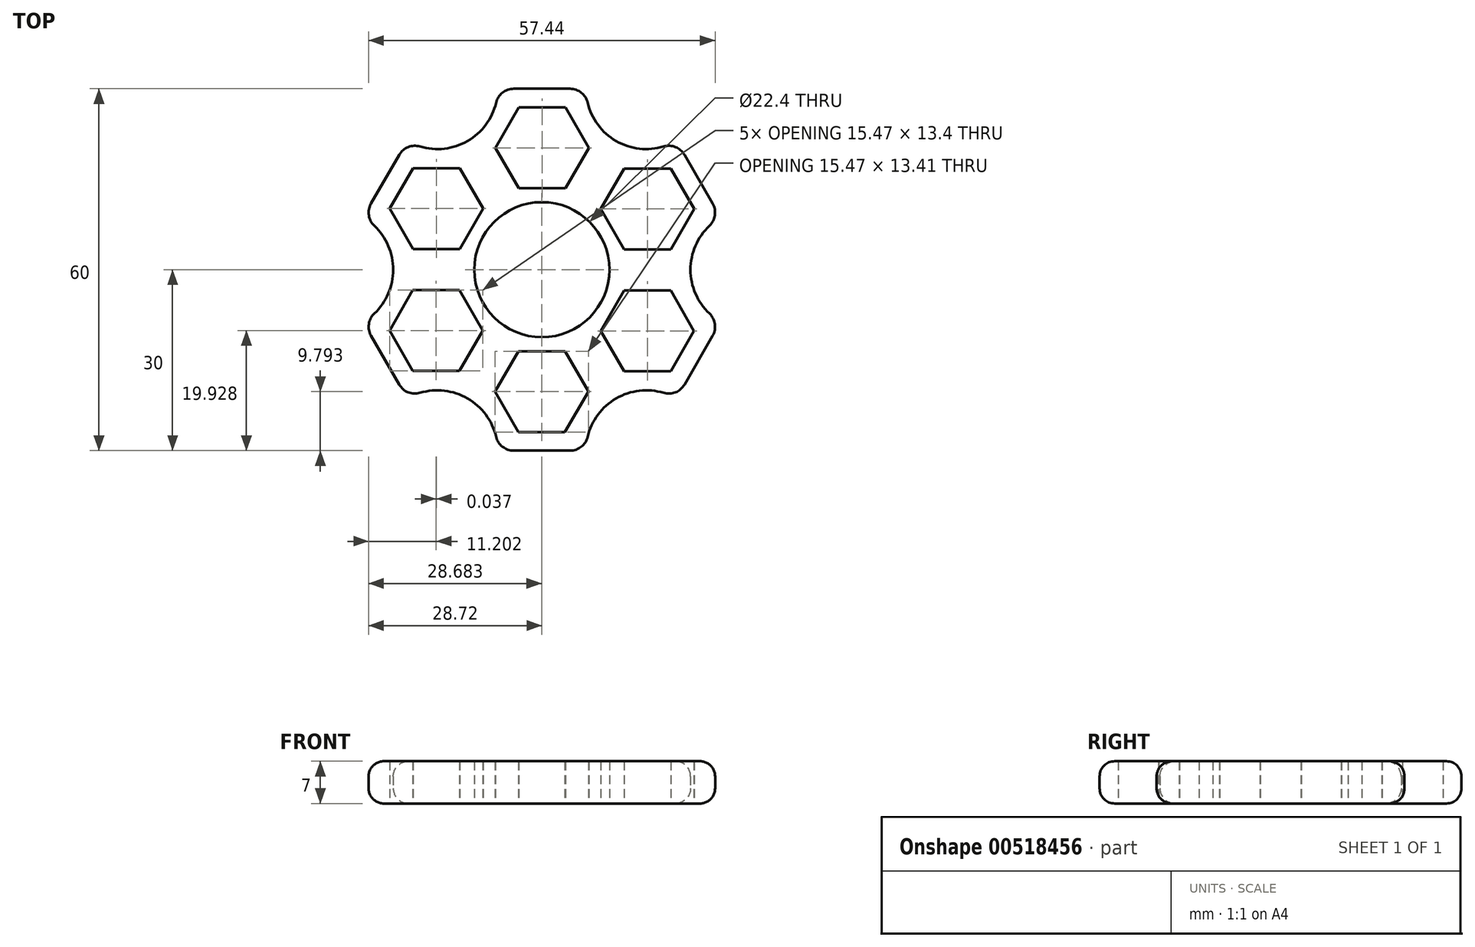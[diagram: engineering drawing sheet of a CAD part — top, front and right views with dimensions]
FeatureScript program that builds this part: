
annotation { "Feature Type Name" : "Feature", "Feature Type Description" : "" }
export const myFeature = defineFeature(function(context is Context, id is Id, definition is map)
    precondition{}
    {
        {
            var Q0;
            Q0=qCreatedBy(makeId("Top.planeOp"),FACE);
            var sketch = newSketch(context, id + "F0", { "sketchPlane" : qUnion([Q0])});
            skCircle(sketch, "E0", {"center": v(0, 0) * mm, "radius": 11.2 * mm});
            skCircle(sketch, "E1.cCircle", {"center": v(0, 0) * mm, "radius": 17.5 * mm, "construction": true});
            skLineSegment(sketch, "E1.0", {"start": v(0.04, 20.2) * mm, "end": v(17.52, 10.07) * mm});
            skLineSegment(sketch, "E1.1", {"start": v(17.52, 10.07) * mm, "end": v(17.48, -10.14) * mm});
            skLineSegment(sketch, "E1.2", {"start": v(17.48, -10.14) * mm, "end": v(-0.04, -20.2) * mm});
            skLineSegment(sketch, "E1.3", {"start": v(-0.04, -20.2) * mm, "end": v(-17.52, -10.07) * mm});
            skLineSegment(sketch, "E1.4", {"start": v(-17.52, -10.07) * mm, "end": v(-17.48, 10.14) * mm});
            skLineSegment(sketch, "E1.5", {"start": v(-17.48, 10.14) * mm, "end": v(0.04, 20.2) * mm});
            skPoint(sketch, "E1.0.midPoint", {"position": v(8.78, 15.14) * mm});
            skCircle(sketch, "E2.cCircle", {"center": v(0.04, 20.2) * mm, "radius": 6.7 * mm, "construction": true});
            skLineSegment(sketch, "E2.0", {"start": v(-3.83, 26.9) * mm, "end": v(3.9, 26.9) * mm});
            skLineSegment(sketch, "E2.1", {"start": v(3.9, 26.9) * mm, "end": v(7.77, 20.2) * mm});
            skLineSegment(sketch, "E2.2", {"start": v(7.77, 20.2) * mm, "end": v(3.9, 13.5) * mm});
            skLineSegment(sketch, "E2.3", {"start": v(3.9, 13.5) * mm, "end": v(-3.83, 13.5) * mm});
            skLineSegment(sketch, "E2.4", {"start": v(-3.83, 13.5) * mm, "end": v(-7.7, 20.2) * mm});
            skLineSegment(sketch, "E2.5", {"start": v(-7.7, 20.2) * mm, "end": v(-3.83, 26.9) * mm});
            skPoint(sketch, "E2.0.midPoint", {"position": v(0.04, 26.9) * mm});
            skCircle(sketch, "E3.cCircle", {"center": v(-17.48, 10.14) * mm, "radius": 6.7 * mm, "construction": true});
            skLineSegment(sketch, "E3.0", {"start": v(-21.35, 16.84) * mm, "end": v(-13.61, 16.84) * mm});
            skLineSegment(sketch, "E3.1", {"start": v(-13.61, 16.84) * mm, "end": v(-9.75, 10.14) * mm});
            skLineSegment(sketch, "E3.2", {"start": v(-9.75, 10.14) * mm, "end": v(-13.61, 3.44) * mm});
            skLineSegment(sketch, "E3.3", {"start": v(-13.61, 3.44) * mm, "end": v(-21.35, 3.44) * mm});
            skLineSegment(sketch, "E3.4", {"start": v(-21.35, 3.44) * mm, "end": v(-25.22, 10.14) * mm});
            skLineSegment(sketch, "E3.5", {"start": v(-25.22, 10.14) * mm, "end": v(-21.35, 16.84) * mm});
            skPoint(sketch, "E3.0.midPoint", {"position": v(-17.48, 16.84) * mm});
            skCircle(sketch, "E4.cCircle", {"center": v(-17.52, -10.07) * mm, "radius": 6.7 * mm, "construction": true});
            skLineSegment(sketch, "E4.0", {"start": v(-13.65, -16.77) * mm, "end": v(-21.39, -16.77) * mm});
            skLineSegment(sketch, "E4.1", {"start": v(-21.39, -16.77) * mm, "end": v(-25.25, -10.07) * mm});
            skLineSegment(sketch, "E4.2", {"start": v(-25.25, -10.07) * mm, "end": v(-21.39, -3.37) * mm});
            skLineSegment(sketch, "E4.3", {"start": v(-21.39, -3.37) * mm, "end": v(-13.65, -3.37) * mm});
            skLineSegment(sketch, "E4.4", {"start": v(-13.65, -3.37) * mm, "end": v(-9.78, -10.07) * mm});
            skLineSegment(sketch, "E4.5", {"start": v(-9.78, -10.07) * mm, "end": v(-13.65, -16.77) * mm});
            skPoint(sketch, "E4.0.midPoint", {"position": v(-17.52, -16.77) * mm});
            skCircle(sketch, "E5.cCircle", {"center": v(17.48, -10.14) * mm, "radius": 6.7 * mm, "construction": true});
            skLineSegment(sketch, "E5.0", {"start": v(21.35, -16.84) * mm, "end": v(13.61, -16.84) * mm});
            skLineSegment(sketch, "E5.1", {"start": v(13.61, -16.84) * mm, "end": v(9.75, -10.14) * mm});
            skLineSegment(sketch, "E5.2", {"start": v(9.75, -10.14) * mm, "end": v(13.61, -3.44) * mm});
            skLineSegment(sketch, "E5.3", {"start": v(13.61, -3.44) * mm, "end": v(21.35, -3.44) * mm});
            skLineSegment(sketch, "E5.4", {"start": v(21.35, -3.44) * mm, "end": v(25.22, -10.14) * mm});
            skLineSegment(sketch, "E5.5", {"start": v(25.22, -10.14) * mm, "end": v(21.35, -16.84) * mm});
            skPoint(sketch, "E5.0.midPoint", {"position": v(17.48, -16.84) * mm});
            skCircle(sketch, "E6.cCircle", {"center": v(-0.04, -20.2) * mm, "radius": 6.7 * mm, "construction": true});
            skLineSegment(sketch, "E6.0", {"start": v(-3.9, -13.5) * mm, "end": v(3.84, -13.51) * mm});
            skLineSegment(sketch, "E6.1", {"start": v(3.84, -13.51) * mm, "end": v(7.7, -20.22) * mm});
            skLineSegment(sketch, "E6.2", {"start": v(7.7, -20.22) * mm, "end": v(3.82, -26.91) * mm});
            skLineSegment(sketch, "E6.3", {"start": v(3.82, -26.91) * mm, "end": v(-3.92, -26.9) * mm});
            skLineSegment(sketch, "E6.4", {"start": v(-3.92, -26.9) * mm, "end": v(-7.77, -20.2) * mm});
            skLineSegment(sketch, "E6.5", {"start": v(-7.77, -20.2) * mm, "end": v(-3.9, -13.5) * mm});
            skPoint(sketch, "E6.0.midPoint", {"position": v(-0.02, -13.5) * mm});
            skCircle(sketch, "E7.cCircle", {"center": v(17.52, 10.07) * mm, "radius": 6.7 * mm, "construction": true});
            skLineSegment(sketch, "E7.0", {"start": v(21.39, 16.77) * mm, "end": v(25.25, 10.07) * mm});
            skLineSegment(sketch, "E7.1", {"start": v(25.25, 10.07) * mm, "end": v(21.39, 3.37) * mm});
            skLineSegment(sketch, "E7.2", {"start": v(21.39, 3.37) * mm, "end": v(13.65, 3.37) * mm});
            skLineSegment(sketch, "E7.3", {"start": v(13.65, 3.37) * mm, "end": v(9.78, 10.07) * mm});
            skLineSegment(sketch, "E7.4", {"start": v(9.78, 10.07) * mm, "end": v(13.65, 16.77) * mm});
            skLineSegment(sketch, "E7.5", {"start": v(13.65, 16.77) * mm, "end": v(21.39, 16.77) * mm});
            skPoint(sketch, "E7.0.midPoint", {"position": v(23.32, 13.42) * mm});
            skCircle(sketch, "E8.cCircle", {"center": v(0, 0) * mm, "radius": 30 * mm, "construction": true});
            skLineSegment(sketch, "E8.0", {"start": v(-34.64, 0) * mm, "end": v(-17.32, 30) * mm});
            skLineSegment(sketch, "E8.1", {"start": v(-17.32, 30) * mm, "end": v(17.32, 30) * mm});
            skLineSegment(sketch, "E8.2", {"start": v(17.32, 30) * mm, "end": v(34.64, 0) * mm});
            skLineSegment(sketch, "E8.3", {"start": v(34.64, 0) * mm, "end": v(17.32, -30) * mm});
            skLineSegment(sketch, "E8.4", {"start": v(17.32, -30) * mm, "end": v(-17.32, -30) * mm});
            skLineSegment(sketch, "E8.5", {"start": v(-17.32, -30) * mm, "end": v(-34.64, 0) * mm});
            skPoint(sketch, "E8.0.midPoint", {"position": v(-25.98, 15) * mm});
            skCircle(sketch, "E9", {"center": v(-17.32, 30) * mm, "radius": 10 * mm});
            skCircle(sketch, "E10", {"center": v(17.32, 30) * mm, "radius": 10 * mm});
            skCircle(sketch, "E11", {"center": v(34.64, 0) * mm, "radius": 10 * mm});
            skCircle(sketch, "E12", {"center": v(17.32, -30) * mm, "radius": 10 * mm});
            skCircle(sketch, "E13", {"center": v(-17.32, -30) * mm, "radius": 10 * mm});
            skCircle(sketch, "E14", {"center": v(-34.64, 0) * mm, "radius": 10 * mm});
            skSolve(sketch);
        }
        {
            var Q0;
            Q0=makeQuery(id+"F0.imprint","IMPRINT",FACE,{"disambiguationData":[TD([[makeQuery(id+"F0.imprint","IMPRINT",EDGE,{"derivedFrom":sQuery(id+"F0.wireOp",EDGE,"E2.0")}),1.0]])]});
            var Q1;
            Q1=makeQuery(id+"F0.imprint","IMPRINT",FACE,{"disambiguationData":[TD([[makeQuery(id+"F0.imprint","IMPRINT",EDGE,{"derivedFrom":sQuery(id+"F0.wireOp",EDGE,"E0")}),-1.0]])]});
            extrude(context, id + "F1", {"entities" : qUnion([Q0, Q1]), "depth" : 7 * mm, "offsetDistance" : 25 * mm});
        }
        {
            var Q0;
            Q0=makeQuery(id+"F1.opExtrude","CAP_EDGE",EDGE,{"disambiguationData":[OSD([sQuery(id+"F0.wireOp",EDGE,"E8.5")])],"isStart":false});
            var Q1;
            Q1=makeQuery(id+"F1.opExtrude","CAP_EDGE",EDGE,{"disambiguationData":[OSD([sQuery(id+"F0.wireOp",EDGE,"E13")])],"isStart":false});
            var Q2;
            Q2=makeQuery(id+"F1.opExtrude","CAP_EDGE",EDGE,{"disambiguationData":[OSD([sQuery(id+"F0.wireOp",EDGE,"E8.4")])],"isStart":false});
            var Q3;
            Q3=makeQuery(id+"F1.opExtrude","CAP_EDGE",EDGE,{"disambiguationData":[OSD([sQuery(id+"F0.wireOp",EDGE,"E12")])],"isStart":false});
            var Q4;
            Q4=makeQuery(id+"F1.opExtrude","CAP_EDGE",EDGE,{"disambiguationData":[OSD([sQuery(id+"F0.wireOp",EDGE,"E8.3")])],"isStart":false});
            var Q5;
            Q5=makeQuery(id+"F1.opExtrude","CAP_EDGE",EDGE,{"disambiguationData":[OSD([sQuery(id+"F0.wireOp",EDGE,"E11")])],"isStart":false});
            var Q6;
            Q6=makeQuery(id+"F1.opExtrude","CAP_EDGE",EDGE,{"disambiguationData":[OSD([sQuery(id+"F0.wireOp",EDGE,"E8.2")])],"isStart":false});
            var Q7;
            Q7=makeQuery(id+"F1.opExtrude","CAP_EDGE",EDGE,{"disambiguationData":[OSD([sQuery(id+"F0.wireOp",EDGE,"E10")])],"isStart":false});
            var Q8;
            Q8=makeQuery(id+"F1.opExtrude","CAP_EDGE",EDGE,{"disambiguationData":[OSD([sQuery(id+"F0.wireOp",EDGE,"E8.1")])],"isStart":false});
            var Q9;
            Q9=makeQuery(id+"F1.opExtrude","CAP_EDGE",EDGE,{"disambiguationData":[OSD([sQuery(id+"F0.wireOp",EDGE,"E9")])],"isStart":false});
            var Q10;
            Q10=makeQuery(id+"F1.opExtrude","CAP_EDGE",EDGE,{"disambiguationData":[OSD([sQuery(id+"F0.wireOp",EDGE,"E8.0")])],"isStart":false});
            var Q11;
            Q11=makeQuery(id+"F1.opExtrude","CAP_EDGE",EDGE,{"disambiguationData":[OSD([sQuery(id+"F0.wireOp",EDGE,"E14")])],"isStart":false});
            var Q12;
            Q12=makeQuery(id+"F1.opExtrude","CAP_EDGE",EDGE,{"disambiguationData":[OSD([sQuery(id+"F0.wireOp",EDGE,"E8.4")])],"isStart":true});
            var Q13;
            Q13=makeQuery(id+"F1.opExtrude","CAP_EDGE",EDGE,{"disambiguationData":[OSD([sQuery(id+"F0.wireOp",EDGE,"E12")])],"isStart":true});
            var Q14;
            Q14=makeQuery(id+"F1.opExtrude","CAP_EDGE",EDGE,{"disambiguationData":[OSD([sQuery(id+"F0.wireOp",EDGE,"E8.3")])],"isStart":true});
            var Q15;
            Q15=makeQuery(id+"F1.opExtrude","CAP_EDGE",EDGE,{"disambiguationData":[OSD([sQuery(id+"F0.wireOp",EDGE,"E11")])],"isStart":true});
            var Q16;
            Q16=makeQuery(id+"F1.opExtrude","CAP_EDGE",EDGE,{"disambiguationData":[OSD([sQuery(id+"F0.wireOp",EDGE,"E8.2")])],"isStart":true});
            var Q17;
            Q17=makeQuery(id+"F1.opExtrude","CAP_EDGE",EDGE,{"disambiguationData":[OSD([sQuery(id+"F0.wireOp",EDGE,"E10")])],"isStart":true});
            var Q18;
            Q18=makeQuery(id+"F1.opExtrude","CAP_EDGE",EDGE,{"disambiguationData":[OSD([sQuery(id+"F0.wireOp",EDGE,"E8.1")])],"isStart":true});
            var Q19;
            Q19=makeQuery(id+"F1.opExtrude","CAP_EDGE",EDGE,{"disambiguationData":[OSD([sQuery(id+"F0.wireOp",EDGE,"E9")])],"isStart":true});
            var Q20;
            Q20=makeQuery(id+"F1.opExtrude","CAP_EDGE",EDGE,{"disambiguationData":[OSD([sQuery(id+"F0.wireOp",EDGE,"E8.0")])],"isStart":true});
            var Q21;
            Q21=makeQuery(id+"F1.opExtrude","CAP_EDGE",EDGE,{"disambiguationData":[OSD([sQuery(id+"F0.wireOp",EDGE,"E14")])],"isStart":true});
            var Q22;
            Q22=makeQuery(id+"F1.opExtrude","CAP_EDGE",EDGE,{"disambiguationData":[OSD([sQuery(id+"F0.wireOp",EDGE,"E8.5")])],"isStart":true});
            var Q23;
            Q23=makeQuery(id+"F1.opExtrude","CAP_EDGE",EDGE,{"disambiguationData":[OSD([sQuery(id+"F0.wireOp",EDGE,"E13")])],"isStart":true});
            fillet(context, id + "F2", {"entities" : qUnion([Q0, Q1, Q2, Q3, Q4, Q5, Q6, Q7, Q8, Q9, Q10, Q11, Q12, Q13, Q14, Q15, Q16, Q17, Q18, Q19, Q20, Q21, Q22, Q23]), "radius" : 2.5 * mm, "tangentPropagation" : true, "allowEdgeOverflow" : false});
        }
        {
            var Q0;
            Q0=makeQuery(id+"F1.opExtrude","SWEPT_EDGE",EDGE,{"disambiguationData":[OSD([sQuery(id+"F0.wireOp",EDGE,"E8.1"),sQuery(id+"F0.wireOp",EDGE,"E9")])]});
            var Q1;
            Q1=makeQuery(id+"F1.opExtrude","SWEPT_EDGE",EDGE,{"disambiguationData":[OSD([sQuery(id+"F0.wireOp",EDGE,"E8.1"),sQuery(id+"F0.wireOp",EDGE,"E10")])]});
            var Q2;
            Q2=makeQuery(id+"F1.opExtrude","SWEPT_EDGE",EDGE,{"disambiguationData":[OSD([sQuery(id+"F0.wireOp",EDGE,"E8.2"),sQuery(id+"F0.wireOp",EDGE,"E10")])]});
            var Q3;
            Q3=makeQuery(id+"F1.opExtrude","SWEPT_EDGE",EDGE,{"disambiguationData":[OSD([sQuery(id+"F0.wireOp",EDGE,"E8.0"),sQuery(id+"F0.wireOp",EDGE,"E9")])]});
            var Q4;
            Q4=makeQuery(id+"F1.opExtrude","SWEPT_EDGE",EDGE,{"disambiguationData":[OSD([sQuery(id+"F0.wireOp",EDGE,"E8.3"),sQuery(id+"F0.wireOp",EDGE,"E11")])]});
            var Q5;
            Q5=makeQuery(id+"F1.opExtrude","SWEPT_EDGE",EDGE,{"disambiguationData":[OSD([sQuery(id+"F0.wireOp",EDGE,"E8.3"),sQuery(id+"F0.wireOp",EDGE,"E12")])]});
            var Q6;
            Q6=makeQuery(id+"F1.opExtrude","SWEPT_EDGE",EDGE,{"disambiguationData":[OSD([sQuery(id+"F0.wireOp",EDGE,"E8.2"),sQuery(id+"F0.wireOp",EDGE,"E11")])]});
            var Q7;
            Q7=makeQuery(id+"F1.opExtrude","SWEPT_EDGE",EDGE,{"disambiguationData":[OSD([sQuery(id+"F0.wireOp",EDGE,"E8.4"),sQuery(id+"F0.wireOp",EDGE,"E12")])]});
            var Q8;
            Q8=makeQuery(id+"F1.opExtrude","SWEPT_EDGE",EDGE,{"disambiguationData":[OSD([sQuery(id+"F0.wireOp",EDGE,"E8.4"),sQuery(id+"F0.wireOp",EDGE,"E13")])]});
            var Q9;
            Q9=makeQuery(id+"F1.opExtrude","SWEPT_EDGE",EDGE,{"disambiguationData":[OSD([sQuery(id+"F0.wireOp",EDGE,"E8.5"),sQuery(id+"F0.wireOp",EDGE,"E13")])]});
            var Q10;
            Q10=makeQuery(id+"F1.opExtrude","SWEPT_EDGE",EDGE,{"disambiguationData":[OSD([sQuery(id+"F0.wireOp",EDGE,"E8.5"),sQuery(id+"F0.wireOp",EDGE,"E14")])]});
            var Q11;
            Q11=makeQuery(id+"F1.opExtrude","SWEPT_EDGE",EDGE,{"disambiguationData":[OSD([sQuery(id+"F0.wireOp",EDGE,"E8.0"),sQuery(id+"F0.wireOp",EDGE,"E14")])]});
            fillet(context, id + "F3", {"entities" : qUnion([Q0, Q1, Q2, Q3, Q4, Q5, Q6, Q7, Q8, Q9, Q10, Q11]), "radius" : 3 * mm, "tangentPropagation" : true, "allowEdgeOverflow" : false});
        }
    });
